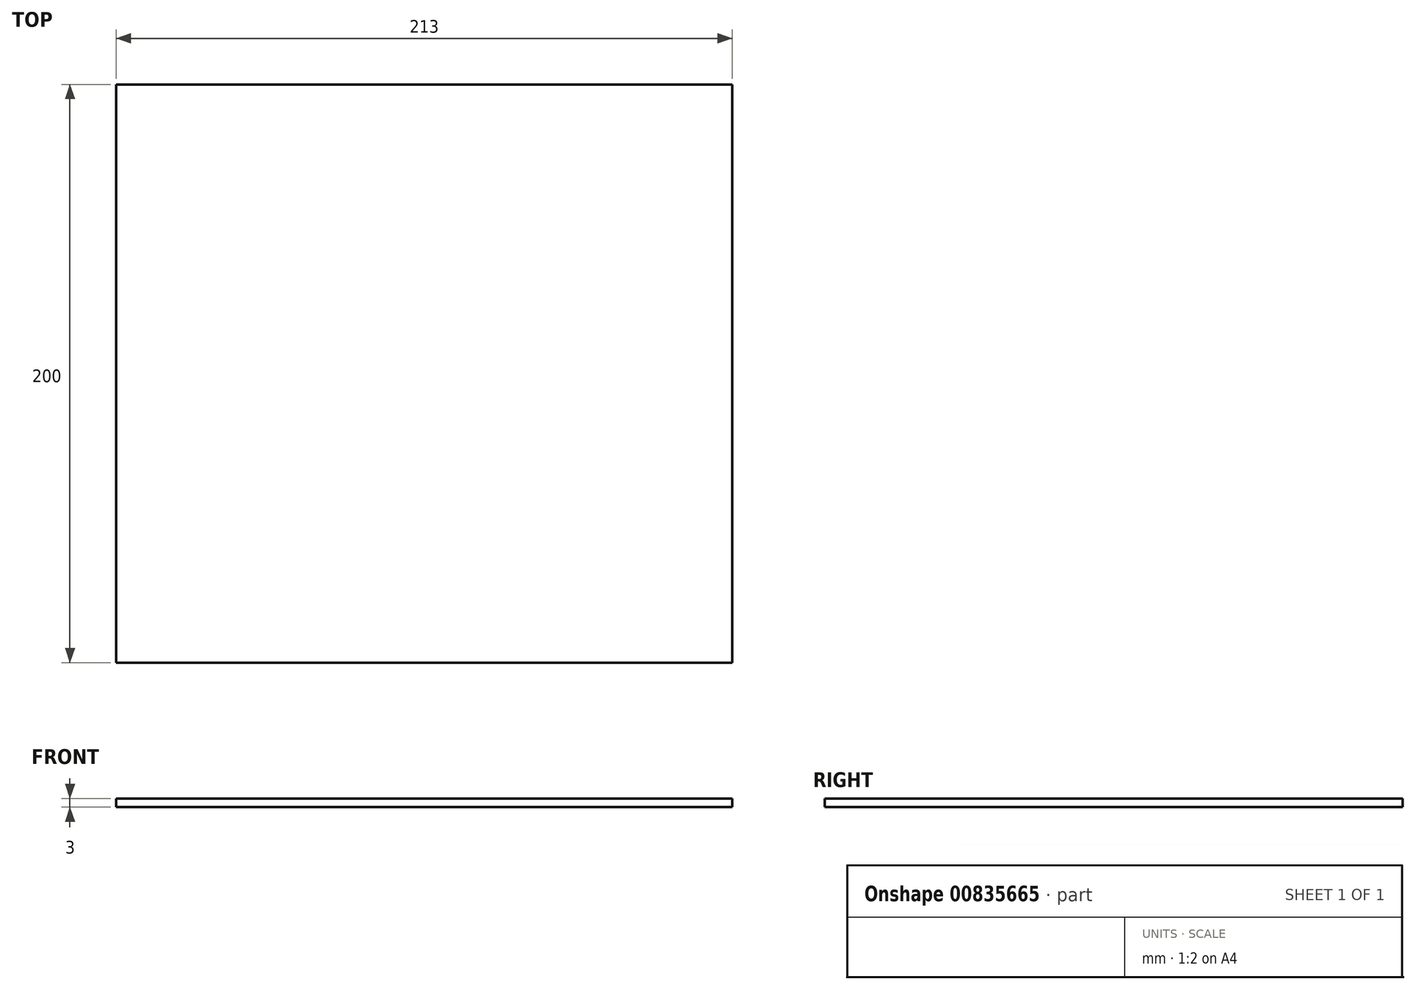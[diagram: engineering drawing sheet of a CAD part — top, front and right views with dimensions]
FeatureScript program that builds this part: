
annotation { "Feature Type Name" : "Feature", "Feature Type Description" : "" }
export const myFeature = defineFeature(function(context is Context, id is Id, definition is map)
    precondition{}
    {
        {
            var Q0;
            Q0=qCreatedBy(makeId("Top.planeOp"),FACE);
            var sketch = newSketch(context, id + "F0", { "sketchPlane" : qUnion([Q0])});
            skLineSegment(sketch, "E0.bottom", {"start": v(-106.5, 100) * mm, "end": v(106.5, 100) * mm});
            skLineSegment(sketch, "E0.top", {"start": v(-106.5, -100) * mm, "end": v(106.5, -100) * mm});
            skLineSegment(sketch, "E0.left", {"start": v(-106.5, 100) * mm, "end": v(-106.5, -100) * mm});
            skLineSegment(sketch, "E0.right", {"start": v(106.5, 100) * mm, "end": v(106.5, -100) * mm});
            skLineSegment(sketch, "E1", {"start": v(-106.5, 100) * mm, "end": v(106.5, -100) * mm, "construction": true});
            skSolve(sketch);
        }
        {
            var Q0;
            Q0=makeQuery(id+"F0.imprint","IMPRINT",FACE,{"disambiguationData":[TD([[makeQuery(id+"F0.imprint","IMPRINT",EDGE,{"derivedFrom":sQuery(id+"F0.wireOp",EDGE,"E0.bottom")}),-1.0]])]});
            extrude(context, id + "F1", {"entities" : qUnion([Q0]), "endBound" : BoundingType.SYMMETRIC, "depth" : 3 * mm, "offsetDistance" : 25.4 * mm});
        }
    });
